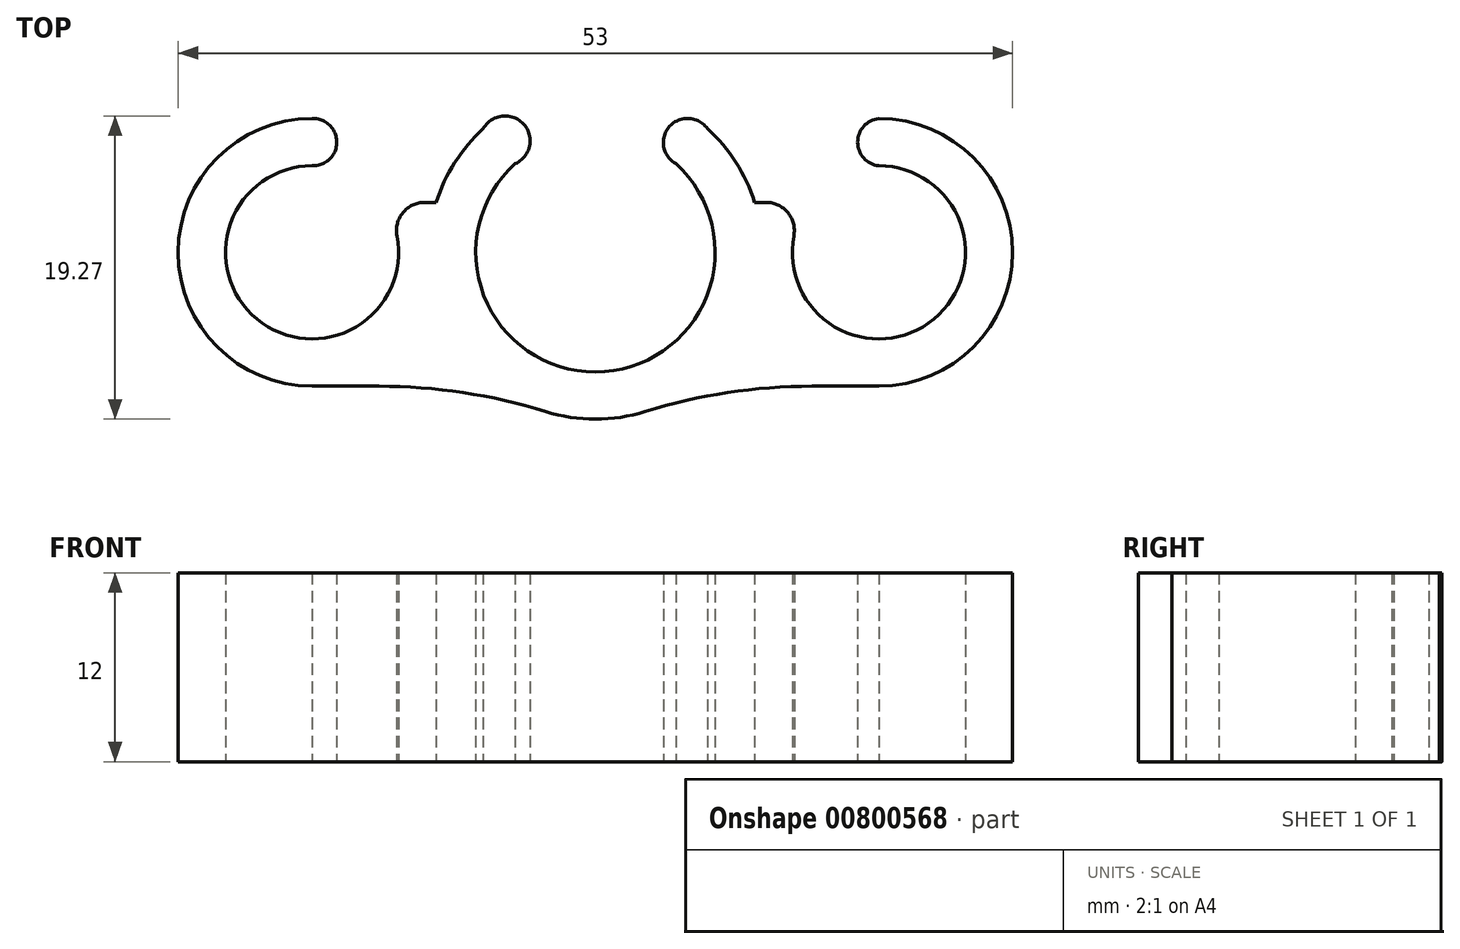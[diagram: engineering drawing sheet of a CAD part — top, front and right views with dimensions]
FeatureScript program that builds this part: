
annotation { "Feature Type Name" : "Feature", "Feature Type Description" : "" }
export const myFeature = defineFeature(function(context is Context, id is Id, definition is map)
    precondition{}
    {
        {
            var Q0;
            Q0=qCreatedBy(makeId("Top.planeOp"),FACE);
            var sketch = newSketch(context, id + "F0", { "sketchPlane" : qUnion([Q0])});
            skLineSegment(sketch, "E0", {"start": v(0, -10.7) * mm, "end": v(0, 12.1) * mm});
            skLineSegment(sketch, "E1.MirrorCS", {"start": v(18, 13.01) * mm, "end": v(18, 5.5) * mm, "construction": true});
            skPoint(sketch, "E2.centerSnap0", {"position": v(0, 0.7) * mm});
            skArc(sketch, "E3", {"start": v(-5.1, 5.63) * mm, "mid": v(0, -7.6) * mm, "end": v(5.1, 5.63) * mm});
            skLineSegment(sketch, "E4", {"start": v(6.91, -4.97) * mm, "end": v(5.75, -4.97) * mm});
            skPoint(sketch, "E5.orphan", {"position": v(13.62, -4.97) * mm});
            skPoint(sketch, "E6.orphan", {"position": v(-18, -6.92) * mm});
            skArc(sketch, "E7.0", {"start": v(-7.12, 7.85) * mm, "mid": v(-8.93, 5.7) * mm, "end": v(-10.11, 3.17) * mm});
            skArc(sketch, "E8", {"start": v(-18, 5.5) * mm, "mid": v(-20.53, -4.88) * mm, "end": v(-13.5, 3.17) * mm});
            skArc(sketch, "E9", {"start": v(13.5, 3.17) * mm, "mid": v(20.53, -4.88) * mm, "end": v(18, 5.5) * mm});
            skPoint(sketch, "E9.centerSnap0", {"position": v(18, 0.7) * mm});
            skArc(sketch, "E10.0", {"start": v(-18, 8.5) * mm, "mid": v(-26.5, 0) * mm, "end": v(-18, -8.5) * mm});
            skLineSegment(sketch, "E11.top", {"start": v(-13.5, 3.17) * mm, "end": v(-10.11, 3.17) * mm});
            skLineSegment(sketch, "E11.left", {"start": v(-18, 10.6) * mm, "end": v(-18, 3.17) * mm});
            skArc(sketch, "E12.trimOffspring", {"start": v(10.11, 3.17) * mm, "mid": v(8.93, 5.7) * mm, "end": v(7.12, 7.85) * mm});
            skLineSegment(sketch, "E13.trimOffspring", {"start": v(-18, 5.5) * mm, "end": v(-18, -11.61) * mm, "construction": true});
            skPoint(sketch, "E14.orphan", {"position": v(-18, 13.01) * mm});
            skLineSegment(sketch, "E15.top", {"start": v(13.5, 3.17) * mm, "end": v(10.11, 3.17) * mm});
            skLineSegment(sketch, "E15.left", {"start": v(18, 8.5) * mm, "end": v(18, 3.17) * mm});
            skArc(sketch, "E16", {"start": v(-18, 5.5) * mm, "mid": v(-16.43, 7) * mm, "end": v(-18, 8.5) * mm});
            skArc(sketch, "E17", {"start": v(18, 8.5) * mm, "mid": v(16.66, 7) * mm, "end": v(18, 5.5) * mm});
            skArc(sketch, "E18", {"start": v(7.12, 7.85) * mm, "mid": v(4.72, 8) * mm, "end": v(5.1, 5.63) * mm});
            skArc(sketch, "E19", {"start": v(-5.1, 5.63) * mm, "mid": v(-4.56, 8.15) * mm, "end": v(-7.12, 7.85) * mm});
            skLineSegment(sketch, "E20.trimOffspring", {"start": v(18, 3.17) * mm, "end": v(18, -11.61) * mm, "construction": true});
            skLineSegment(sketch, "E21", {"start": v(-18, -8.5) * mm, "end": v(-6.33, -8.5) * mm});
            skLineSegment(sketch, "E22", {"start": v(18, -8.5) * mm, "end": v(6.33, -8.5) * mm});
            skArc(sketch, "E23.trimOffspring", {"start": v(18, -8.5) * mm, "mid": v(26.5, 0) * mm, "end": v(18, 8.5) * mm});
            skArc(sketch, "E24.trimOffspring", {"start": v(-6.33, -8.5) * mm, "mid": v(0, -10.6) * mm, "end": v(6.33, -8.5) * mm});
            skSolve(sketch);
        }
        {
            var Q0;
            {var subQ5=sQuery(id+"F0.wireOp",EDGE,"E9");Q0=makeQuery(id+"F0.imprint","IMPRINT",FACE,{"disambiguationData":[TD([[makeQuery(id+"F0.imprint","IMPRINT",EDGE,{"derivedFrom":subQ5}),-1.0]])]});}
            var Q1;
            {var subQ0=sQuery(id+"F0.wireOp",EDGE,"E17");Q1=makeQuery(id+"F0.imprint","IMPRINT",FACE,{"disambiguationData":[TD([[makeQuery(id+"F0.imprint","IMPRINT",EDGE,{"derivedFrom":subQ0}),1.0]])]});}
            var Q2;
            Q2=makeQuery(id+"F0.imprint","IMPRINT",FACE,{"disambiguationData":[TD([[makeQuery(id+"F0.imprint","IMPRINT",EDGE,{"derivedFrom":sQuery(id+"F0.wireOp",EDGE,"E7.0")}),1.0]])]});
            var Q3;
            {var subQ0=sQuery(id+"F0.wireOp",EDGE,"E16");Q3=makeQuery(id+"F0.imprint","IMPRINT",FACE,{"disambiguationData":[TD([[makeQuery(id+"F0.imprint","IMPRINT",EDGE,{"derivedFrom":subQ0}),1.0]])]});}
            extrude(context, id + "F1", {"entities" : qUnion([Q0, Q1, Q2, Q3]), "depth" : 12 * mm, "offsetDistance" : 25 * mm});
        }
        {
            var Q0;
            Q0=makeQuery(id+"F1.opExtrude","SWEPT_EDGE",EDGE,{"disambiguationData":[OSD([sQuery(id+"F0.wireOp",EDGE,"E21"),sQuery(id+"F0.wireOp",EDGE,"E24.trimOffspring")])]});
            var Q1;
            Q1=makeQuery(id+"F1.opExtrude","SWEPT_EDGE",EDGE,{"disambiguationData":[OSD([sQuery(id+"F0.wireOp",EDGE,"E22"),sQuery(id+"F0.wireOp",EDGE,"E24.trimOffspring")])]});
            fillet(context, id + "F2", {"entities" : qUnion([Q0, Q1]), "radius" : 35.5 * mm, "tangentPropagation" : true, "allowEdgeOverflow" : false});
        }
        {
            var Q0;
            Q0=makeQuery(id+"F1.opExtrude","SWEPT_EDGE",EDGE,{"disambiguationData":[OSD([sQuery(id+"F0.wireOp",EDGE,"E8"),sQuery(id+"F0.wireOp",EDGE,"E11.top")])]});
            var Q1;
            Q1=makeQuery(id+"F1.opExtrude","SWEPT_EDGE",EDGE,{"disambiguationData":[OSD([sQuery(id+"F0.wireOp",EDGE,"E9"),sQuery(id+"F0.wireOp",EDGE,"E15.top")])]});
            fillet(context, id + "F3", {"entities" : qUnion([Q0, Q1]), "radius" : 1.79 * mm, "tangentPropagation" : true, "allowEdgeOverflow" : false});
        }
    });
